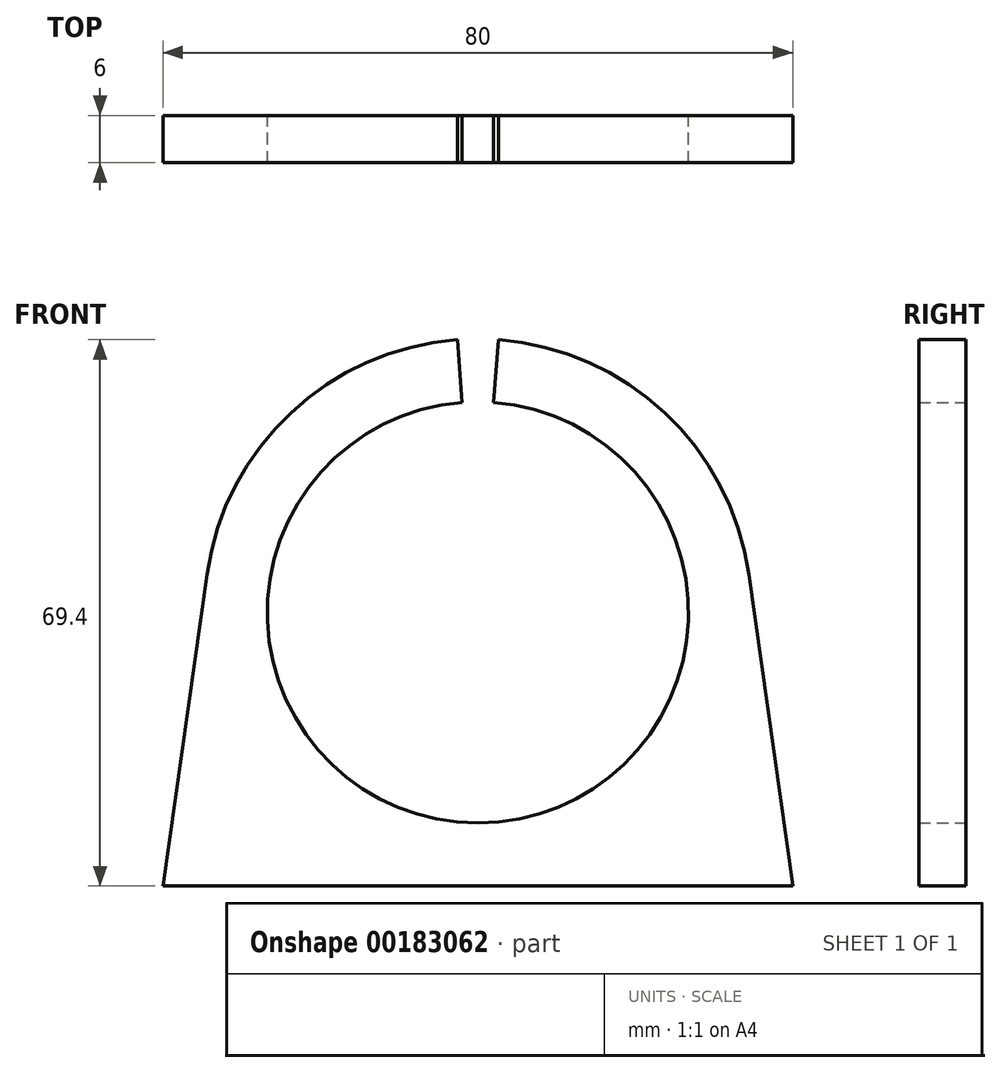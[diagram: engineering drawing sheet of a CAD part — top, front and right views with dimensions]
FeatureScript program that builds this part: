
annotation { "Feature Type Name" : "Feature", "Feature Type Description" : "" }
export const myFeature = defineFeature(function(context is Context, id is Id, definition is map)
    precondition{}
    {
        {
            var Q0;
            Q0=qCreatedBy(makeId("Front.planeOp"),FACE);
            var sketch = newSketch(context, id + "F0", { "sketchPlane" : qUnion([Q0])});
            skLineSegment(sketch, "E0", {"start": v(-34.4, 39.6) * mm, "end": v(-40, 0) * mm});
            skArc(sketch, "E1", {"start": v(-2.6, 69.4) * mm, "mid": v(-23.76, 60.11) * mm, "end": v(-34.4, 39.6) * mm});
            skLineSegment(sketch, "E2", {"start": v(0, 0) * mm, "end": v(-40, 0) * mm});
            skArc(sketch, "E3", {"start": v(-2, 61.43) * mm, "mid": v(-26.73, 33.75) * mm, "end": v(0, 8) * mm});
            skLineSegment(sketch, "E4", {"start": v(-2, 61.43) * mm, "end": v(-2.6, 69.4) * mm});
            skLineSegment(sketch, "E5", {"start": v(0, 8) * mm, "end": v(0, 0) * mm});
            skSolve(sketch);
        }
        {
            var Q0;
            Q0=makeQuery(id+"F0.imprint","IMPRINT",FACE,{"disambiguationData":[TD([[makeQuery(id+"F0.imprint","IMPRINT",EDGE,{"derivedFrom":sQuery(id+"F0.wireOp",EDGE,"E0")}),1.0]])]});
            extrude(context, id + "F1", {"entities" : qUnion([Q0]), "depth" : 6 * mm});
        }
        {
            var Q0;
            Q0=makeQuery(id+"F1.opExtrude","SWEPT_BODY",BODY,{"disambiguationData":[OSD([sQuery(id+"F0.wireOp",EDGE,"E0"),sQuery(id+"F0.wireOp",EDGE,"E1"),sQuery(id+"F0.wireOp",EDGE,"E2"),sQuery(id+"F0.wireOp",EDGE,"E3"),sQuery(id+"F0.wireOp",EDGE,"E4"),sQuery(id+"F0.wireOp",EDGE,"E5")])]});
            var Q1;
            Q1=qCreatedBy(makeId("Right.planeOp"),FACE);
            mirror(context, id + "F2", {"operationType" : NewBodyOperationType.ADD, "entities" : qUnion([Q0]), "mirrorPlane" : qUnion([Q1])});
        }
    });
